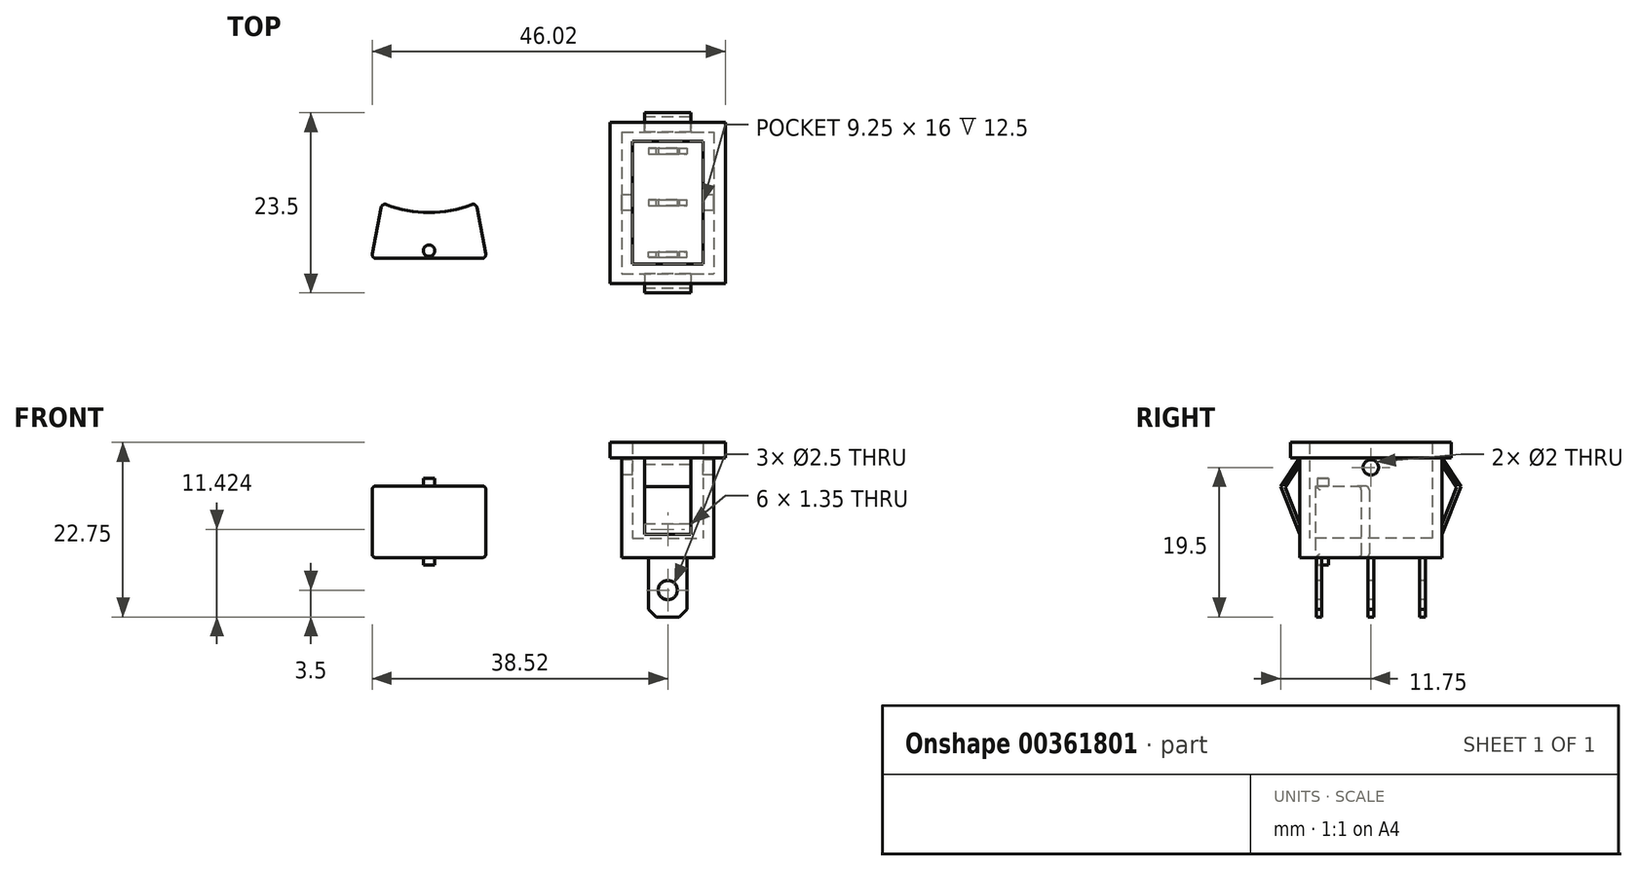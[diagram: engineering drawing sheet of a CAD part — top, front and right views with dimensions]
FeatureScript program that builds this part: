
annotation { "Feature Type Name" : "Feature", "Feature Type Description" : "" }
export const myFeature = defineFeature(function(context is Context, id is Id, definition is map)
    precondition{}
    {
        {
            var Q0;
            Q0=qCreatedBy(makeId("Top.planeOp"),FACE);
            var sketch = newSketch(context, id + "F0", { "sketchPlane" : qUnion([Q0])});
            skLineSegment(sketch, "E0.bottom", {"start": v(-6, 9.25) * mm, "end": v(6, 9.25) * mm});
            skLineSegment(sketch, "E0.top", {"start": v(-6, -9.25) * mm, "end": v(6, -9.25) * mm});
            skLineSegment(sketch, "E0.left", {"start": v(-6, 9.25) * mm, "end": v(-6, -9.25) * mm});
            skLineSegment(sketch, "E0.right", {"start": v(6, 9.25) * mm, "end": v(6, -9.25) * mm});
            skPoint(sketch, "E0.middle", {"position": v(0, 0) * mm});
            skLineSegment(sketch, "E1.bottom", {"start": v(-7.5, 10.5) * mm, "end": v(7.5, 10.5) * mm});
            skLineSegment(sketch, "E1.top", {"start": v(-7.5, -10.5) * mm, "end": v(7.5, -10.5) * mm});
            skLineSegment(sketch, "E1.left", {"start": v(-7.5, 10.5) * mm, "end": v(-7.5, -10.5) * mm});
            skLineSegment(sketch, "E1.right", {"start": v(7.5, 10.5) * mm, "end": v(7.5, -10.5) * mm});
            skLineSegment(sketch, "E2.bottom", {"start": v(-2.5, 0.37) * mm, "end": v(2.5, 0.37) * mm});
            skLineSegment(sketch, "E2.top", {"start": v(-2.5, -0.37) * mm, "end": v(2.5, -0.37) * mm});
            skLineSegment(sketch, "E2.left", {"start": v(-2.5, 0.37) * mm, "end": v(-2.5, -0.37) * mm});
            skLineSegment(sketch, "E2.right", {"start": v(2.5, 0.37) * mm, "end": v(2.5, -0.37) * mm});
            skLineSegment(sketch, "E3.bottom", {"start": v(-2.5, 7.12) * mm, "end": v(2.5, 7.12) * mm});
            skLineSegment(sketch, "E3.top", {"start": v(-2.5, 6.38) * mm, "end": v(2.5, 6.37) * mm});
            skLineSegment(sketch, "E3.left", {"start": v(-2.5, 7.12) * mm, "end": v(-2.5, 6.37) * mm});
            skLineSegment(sketch, "E3.right", {"start": v(2.5, 7.12) * mm, "end": v(2.5, 6.37) * mm});
            skPoint(sketch, "E3.middle", {"position": v(0, 6.75) * mm});
            skLineSegment(sketch, "E4.MirrorCS", {"start": v(-2.5, -6.38) * mm, "end": v(2.5, -6.37) * mm});
            skLineSegment(sketch, "E5.MirrorCS", {"start": v(2.5, -7.12) * mm, "end": v(2.5, -6.37) * mm});
            skLineSegment(sketch, "E6.MirrorCS", {"start": v(-2.5, -7.12) * mm, "end": v(2.5, -7.12) * mm});
            skPoint(sketch, "E7.MirrorP", {"position": v(0, -6.75) * mm});
            skLineSegment(sketch, "E8.MirrorCS", {"start": v(-2.5, -7.12) * mm, "end": v(-2.5, -6.37) * mm});
            skLineSegment(sketch, "E9.bottom", {"start": v(-4.62, 8) * mm, "end": v(4.63, 8) * mm});
            skLineSegment(sketch, "E9.top", {"start": v(-4.63, -8) * mm, "end": v(4.62, -8) * mm});
            skLineSegment(sketch, "E9.left", {"start": v(-4.62, 8) * mm, "end": v(-4.63, -8) * mm});
            skLineSegment(sketch, "E9.right", {"start": v(4.63, 8) * mm, "end": v(4.62, -8) * mm});
            skSolve(sketch);
        }
        {
            var Q0;
            Q0=makeQuery(id+"F0.imprint","IMPRINT",FACE,{"disambiguationData":[TD([[makeQuery(id+"F0.imprint","IMPRINT",EDGE,{"derivedFrom":sQuery(id+"F0.wireOp",EDGE,"E2.bottom")}),-1.0]])]});
            var Q1;
            Q1=makeQuery(id+"F0.imprint","IMPRINT",FACE,{"disambiguationData":[TD([[makeQuery(id+"F0.imprint","IMPRINT",EDGE,{"derivedFrom":sQuery(id+"F0.wireOp",EDGE,"E3.bottom")}),-1.0]])]});
            var Q2;
            Q2=makeQuery(id+"F0.imprint","IMPRINT",FACE,{"disambiguationData":[TD([[makeQuery(id+"F0.imprint","IMPRINT",EDGE,{"derivedFrom":sQuery(id+"F0.wireOp",EDGE,"E4.MirrorCS")}),-1.0]])]});
            extrude(context, id + "F1", {"entities" : qUnion([Q0, Q1, Q2]), "oppositeDirection" : true, "depth" : 7.75 * mm, "offsetDistance" : 25 * mm});
        }
        {
            var Q0;
            Q0=makeQuery(id+"F0.imprint","IMPRINT",FACE,{"disambiguationData":[TD([[makeQuery(id+"F0.imprint","IMPRINT",EDGE,{"derivedFrom":sQuery(id+"F0.wireOp",EDGE,"E0.bottom")}),-1.0]])]});
            extrude(context, id + "F2", {"entities" : qUnion([Q0]), "depth" : 13 * mm, "offsetDistance" : 25 * mm});
        }
        {
            var Q0;
            Q0=makeQuery(id+"F0.imprint","IMPRINT",FACE,{"disambiguationData":[TD([[makeQuery(id+"F0.imprint","IMPRINT",EDGE,{"derivedFrom":sQuery(id+"F0.wireOp",EDGE,"E2.bottom")}),1.0]])]});
            var Q1;
            Q1=makeQuery(id+"F0.imprint","IMPRINT",FACE,{"disambiguationData":[TD([[makeQuery(id+"F0.imprint","IMPRINT",EDGE,{"derivedFrom":sQuery(id+"F0.wireOp",EDGE,"E3.bottom")}),-1.0]])]});
            var Q2;
            Q2=makeQuery(id+"F0.imprint","IMPRINT",FACE,{"disambiguationData":[TD([[makeQuery(id+"F0.imprint","IMPRINT",EDGE,{"derivedFrom":sQuery(id+"F0.wireOp",EDGE,"E2.bottom")}),-1.0]])]});
            var Q3;
            Q3=makeQuery(id+"F0.imprint","IMPRINT",FACE,{"disambiguationData":[TD([[makeQuery(id+"F0.imprint","IMPRINT",EDGE,{"derivedFrom":sQuery(id+"F0.wireOp",EDGE,"E4.MirrorCS")}),-1.0]])]});
            extrude(context, id + "F3", {"entities" : qUnion([Q0, Q1, Q2, Q3]), "operationType" : NewBodyOperationType.ADD, "depth" : 2.5 * mm, "offsetDistance" : 25 * mm});
        }
        {
            var Q0;
            Q0=makeQuery(id+"F0.imprint","IMPRINT",FACE,{"disambiguationData":[TD([[makeQuery(id+"F0.imprint","IMPRINT",EDGE,{"derivedFrom":sQuery(id+"F0.wireOp",EDGE,"E0.bottom")}),1.0]])]});
            var Q1;
            Q1=makeQuery(id+"F0.imprint","IMPRINT",FACE,{"disambiguationData":[TD([[makeQuery(id+"F0.imprint","IMPRINT",EDGE,{"derivedFrom":sQuery(id+"F0.wireOp",EDGE,"E0.bottom")}),-1.0]])]});
            var Q2;
            Q2=makeQuery(id+"F2.opExtrude","CAP_FACE",FACE,{"disambiguationData":[OSD([sQuery(id+"F0.wireOp",EDGE,"E0.bottom"),sQuery(id+"F0.wireOp",EDGE,"E0.top"),sQuery(id+"F0.wireOp",EDGE,"E0.left"),sQuery(id+"F0.wireOp",EDGE,"E0.right"),sQuery(id+"F0.wireOp",EDGE,"E9.bottom"),sQuery(id+"F0.wireOp",EDGE,"E9.top"),sQuery(id+"F0.wireOp",EDGE,"E9.left"),sQuery(id+"F0.wireOp",EDGE,"E9.right")])],"isStart":false});
            var Q3;
            Q3=makeQuery(id+"F2.opExtrude","CAP_FACE",FACE,{"disambiguationData":[OSD([sQuery(id+"F0.wireOp",EDGE,"E0.bottom"),sQuery(id+"F0.wireOp",EDGE,"E0.top"),sQuery(id+"F0.wireOp",EDGE,"E0.left"),sQuery(id+"F0.wireOp",EDGE,"E0.right"),sQuery(id+"F0.wireOp",EDGE,"E9.bottom"),sQuery(id+"F0.wireOp",EDGE,"E9.top"),sQuery(id+"F0.wireOp",EDGE,"E9.left"),sQuery(id+"F0.wireOp",EDGE,"E9.right")])],"isStart":false});
            extrude(context, id + "F4", {"entities" : qUnion([Q0, Q1]), "operationType" : NewBodyOperationType.ADD, "endBound" : BoundingType.UP_TO_SURFACE, "depth" : 25 * mm, "endBoundEntityFace" : qUnion([Q2]), "hasOffset" : true, "offsetDistance" : 2 * mm, "offsetOppositeDirection" : true, "hasSecondDirection" : true, "secondDirectionBound" : SecondDirectionBoundingType.UP_TO_SURFACE, "secondDirectionOppositeDirection" : false, "secondDirectionDepth" : 25 * mm, "secondDirectionBoundEntityFace" : qUnion([Q3])});
        }
        {
            var Q0;
            Q0=makeQuery(id+"F2.opExtrude","SWEPT_FACE",FACE,{"disambiguationData":[OSD([sQuery(id+"F0.wireOp",EDGE,"E0.left")])]});
            var sketch = newSketch(context, id + "F5", { "sketchPlane" : qUnion([Q0])});
            skCircle(sketch, "E10", {"center": v(0, 11.75) * mm, "radius": 1 * mm});
            skLineSegment(sketch, "E11", {"start": v(-9.25, 13) * mm, "end": v(-11.75, 9.26) * mm});
            skLineSegment(sketch, "E12", {"start": v(-11.75, 9.26) * mm, "end": v(-9.25, 3) * mm});
            skLineSegment(sketch, "E13.0", {"start": v(-11.19, 9.2) * mm, "end": v(-9.25, 4.35) * mm});
            skLineSegment(sketch, "E13.1", {"start": v(-9.25, 12.1) * mm, "end": v(-11.19, 9.2) * mm});
            skLineSegment(sketch, "E14", {"start": v(-9.25, 13) * mm, "end": v(-9.25, 3) * mm});
            skLineSegment(sketch, "E15.MirrorCS", {"start": v(9.25, 12.1) * mm, "end": v(11.19, 9.2) * mm});
            skLineSegment(sketch, "E16.MirrorCS", {"start": v(9.25, 13) * mm, "end": v(11.75, 9.26) * mm});
            skLineSegment(sketch, "E17.MirrorCS", {"start": v(11.19, 9.2) * mm, "end": v(9.25, 4.35) * mm});
            skLineSegment(sketch, "E18.MirrorCS", {"start": v(11.75, 9.26) * mm, "end": v(9.25, 3) * mm});
            skLineSegment(sketch, "E19.MirrorCS", {"start": v(9.25, 13) * mm, "end": v(9.25, 3) * mm});
            skSolve(sketch);
        }
        {
            var Q0;
            Q0=makeQuery(id+"F5.imprint","IMPRINT",FACE,{"disambiguationData":[TD([[makeQuery(id+"F5.imprint","IMPRINT",EDGE,{"derivedFrom":sQuery(id+"F5.wireOp",EDGE,"E10")}),1.0]])]});
            extrude(context, id + "F6", {"entities" : qUnion([Q0]), "operationType" : NewBodyOperationType.REMOVE, "endBound" : BoundingType.THROUGH_ALL, "oppositeDirection" : true, "depth" : 25 * mm, "offsetDistance" : 25 * mm});
        }
        {
            var Q0;
            {var subQ3=sQuery(id+"F5.wireOp",EDGE,"E11");Q0=makeQuery(id+"F5.imprint","IMPRINT",FACE,{"disambiguationData":[TD([[makeQuery(id+"F5.imprint","IMPRINT",EDGE,{"derivedFrom":subQ3}),1.0]])]});}
            var Q1;
            {var subQ3=sQuery(id+"F5.wireOp",EDGE,"E15.MirrorCS");Q1=makeQuery(id+"F5.imprint","IMPRINT",FACE,{"disambiguationData":[TD([[makeQuery(id+"F5.imprint","IMPRINT",EDGE,{"derivedFrom":subQ3}),1.0]])]});}
            var Q2;
            Q2=makeQuery(id+"F2.opExtrude","SWEPT_FACE",FACE,{"disambiguationData":[OSD([sQuery(id+"F0.wireOp",EDGE,"E0.right")])]});
            extrude(context, id + "F7", {"entities" : qUnion([Q0, Q1]), "operationType" : NewBodyOperationType.ADD, "endBound" : BoundingType.UP_TO_SURFACE, "oppositeDirection" : true, "depth" : 25 * mm, "endBoundEntityFace" : qUnion([Q2]), "hasOffset" : true, "offsetDistance" : 3 * mm, "hasSecondDirection" : true, "secondDirectionOppositeDirection" : true, "secondDirectionDepth" : 3 * mm});
        }
        {
            var Q0;
            Q0=qCreatedBy(makeId("Front.planeOp"),FACE);
            var sketch = newSketch(context, id + "F8", { "sketchPlane" : qUnion([Q0])});
            skCircle(sketch, "E20", {"center": v(0, -4.25) * mm, "radius": 1.25 * mm});
            skSolve(sketch);
        }
        {
            var Q0;
            Q0=makeQuery(id+"F8.imprint","IMPRINT",FACE,{"disambiguationData":[TD([[makeQuery(id+"F8.imprint","IMPRINT",EDGE,{"derivedFrom":sQuery(id+"F8.wireOp",EDGE,"E20")}),1.0]])]});
            extrude(context, id + "F9", {"entities" : qUnion([Q0]), "operationType" : NewBodyOperationType.REMOVE, "endBound" : BoundingType.SYMMETRIC, "oppositeDirection" : true, "depth" : 25 * mm, "offsetDistance" : 25 * mm});
        }
        {
            var Q0;
            Q0=makeQuery(id+"F1.opExtrude","CAP_EDGE",EDGE,{"disambiguationData":[OSD([sQuery(id+"F0.wireOp",EDGE,"E3.right")])],"isStart":false});
            var Q1;
            Q1=makeQuery(id+"F1.opExtrude","CAP_EDGE",EDGE,{"disambiguationData":[OSD([sQuery(id+"F0.wireOp",EDGE,"E3.left")])],"isStart":false});
            var Q2;
            Q2=makeQuery(id+"F1.opExtrude","CAP_EDGE",EDGE,{"disambiguationData":[OSD([sQuery(id+"F0.wireOp",EDGE,"E2.left")])],"isStart":false});
            var Q3;
            Q3=makeQuery(id+"F1.opExtrude","CAP_EDGE",EDGE,{"disambiguationData":[OSD([sQuery(id+"F0.wireOp",EDGE,"E8.MirrorCS")])],"isStart":false});
            var Q4;
            Q4=makeQuery(id+"F1.opExtrude","CAP_EDGE",EDGE,{"disambiguationData":[OSD([sQuery(id+"F0.wireOp",EDGE,"E5.MirrorCS")])],"isStart":false});
            var Q5;
            Q5=makeQuery(id+"F1.opExtrude","CAP_EDGE",EDGE,{"disambiguationData":[OSD([sQuery(id+"F0.wireOp",EDGE,"E2.right")])],"isStart":false});
            chamfer(context, id + "F10", {"entities" : qUnion([Q0, Q1, Q2, Q3, Q4, Q5]), "width" : 1 * mm, "tangentPropagation" : true});
        }
        {
            var Q0;
            Q0=qCreatedBy(makeId("Top.planeOp"),FACE);
            var sketch = newSketch(context, id + "F11", { "sketchPlane" : qUnion([Q0])});
            skArc(sketch, "E21", {"start": v(-37.25, 0) * mm, "mid": v(-31.13, -1.25) * mm, "end": v(-25, 0) * mm});
            skLineSegment(sketch, "E22", {"start": v(-37.25, 0) * mm, "end": v(-38.63, -7.25) * mm});
            skLineSegment(sketch, "E23", {"start": v(-38.62, -7.25) * mm, "end": v(-23.63, -7.25) * mm});
            skLineSegment(sketch, "E24", {"start": v(-23.62, -7.25) * mm, "end": v(-25, 0) * mm});
            skCircle(sketch, "E25", {"center": v(-31.13, -6.25) * mm, "radius": 0.75 * mm});
            skPoint(sketch, "E25.centerSnap0", {"position": v(-31.13, -7.25) * mm});
            skSolve(sketch);
        }
        {
            var Q0;
            Q0=makeQuery(id+"F11.imprint","IMPRINT",FACE,{"disambiguationData":[TD([[makeQuery(id+"F11.imprint","IMPRINT",EDGE,{"derivedFrom":sQuery(id+"F11.wireOp",EDGE,"E21")}),-1.0]])]});
            extrude(context, id + "F12", {"entities" : qUnion([Q0]), "depth" : 9.3 * mm, "offsetDistance" : 25 * mm});
        }
        {
            var Q0;
            Q0=makeQuery(id+"F11.imprint","IMPRINT",FACE,{"disambiguationData":[TD([[makeQuery(id+"F11.imprint","IMPRINT",EDGE,{"derivedFrom":sQuery(id+"F11.wireOp",EDGE,"E25")}),1.0]])]});
            var Q1;
            Q1=makeQuery(id+"F12.opExtrude","CAP_FACE",FACE,{"disambiguationData":[OSD([sQuery(id+"F11.wireOp",EDGE,"E21"),sQuery(id+"F11.wireOp",EDGE,"E22"),sQuery(id+"F11.wireOp",EDGE,"E23"),sQuery(id+"F11.wireOp",EDGE,"E24"),sQuery(id+"F11.wireOp",EDGE,"E25")])],"isStart":false});
            extrude(context, id + "F13", {"entities" : qUnion([Q0]), "operationType" : NewBodyOperationType.ADD, "endBound" : BoundingType.UP_TO_SURFACE, "depth" : 25 * mm, "endBoundEntityFace" : qUnion([Q1]), "hasOffset" : true, "offsetDistance" : 1 * mm, "offsetOppositeDirection" : true, "hasSecondDirection" : true, "secondDirectionOppositeDirection" : true, "secondDirectionDepth" : 1 * mm});
        }
        {
            var Q0;
            Q0=makeQuery(id+"F12.opExtrude","SWEPT_FACE",FACE,{"disambiguationData":[OSD([sQuery(id+"F11.wireOp",EDGE,"E21")])]});
            var Q1;
            Q1=makeQuery(id+"F12.opExtrude","SWEPT_FACE",FACE,{"disambiguationData":[OSD([sQuery(id+"F11.wireOp",EDGE,"E22")])]});
            var Q2;
            Q2=makeQuery(id+"F12.opExtrude","SWEPT_FACE",FACE,{"disambiguationData":[OSD([sQuery(id+"F11.wireOp",EDGE,"E24")])]});
            fillet(context, id + "F14", {"entities" : qUnion([Q0, Q1, Q2]), "radius" : .5 * mm, "tangentPropagation" : true, "allowEdgeOverflow" : false});
        }
    });
